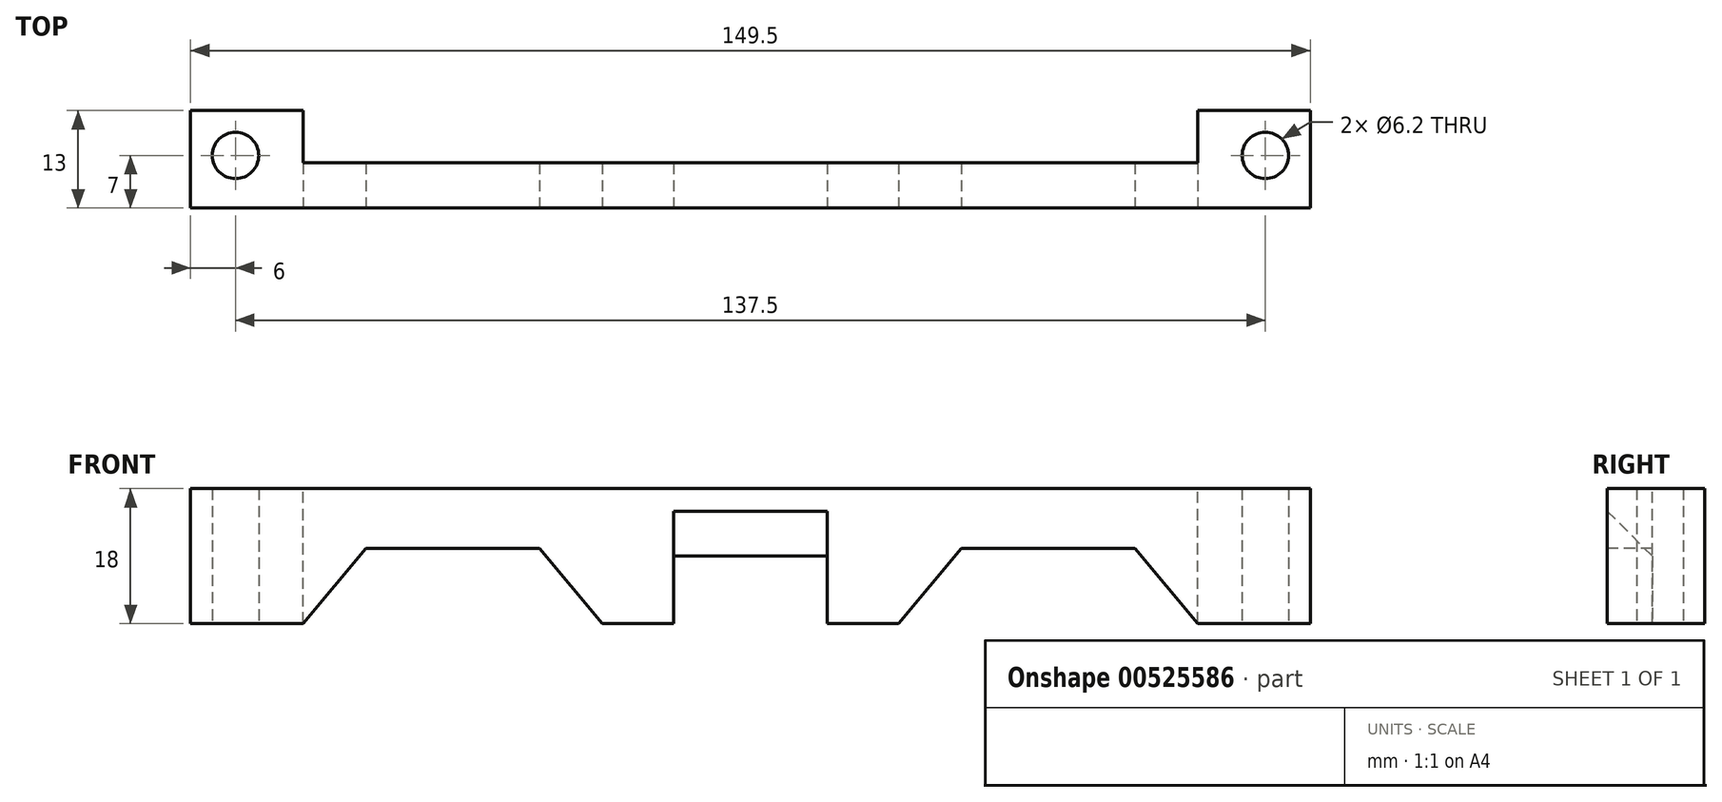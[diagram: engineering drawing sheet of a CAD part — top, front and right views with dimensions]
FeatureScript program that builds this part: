
annotation { "Feature Type Name" : "Feature", "Feature Type Description" : "" }
export const myFeature = defineFeature(function(context is Context, id is Id, definition is map)
    precondition{}
    {
        {
            var Q0;
            Q0=qCreatedBy(makeId("Top.planeOp"),FACE);
            var sketch = newSketch(context, id + "F0", { "sketchPlane" : qUnion([Q0])});
            skLineSegment(sketch, "E0.bottom", {"start": v(74.75, -6.5) * mm, "end": v(-74.75, -6.5) * mm});
            skLineSegment(sketch, "E0.top", {"start": v(74.75, 6.5) * mm, "end": v(-74.75, 6.5) * mm});
            skLineSegment(sketch, "E0.left", {"start": v(74.75, -6.5) * mm, "end": v(74.75, 6.5) * mm});
            skLineSegment(sketch, "E0.right", {"start": v(-74.75, -6.5) * mm, "end": v(-74.75, 6.5) * mm});
            skPoint(sketch, "E0.middle", {"position": v(0, 0) * mm});
            skCircle(sketch, "E1", {"center": v(-68.75, 0.5) * mm, "radius": 3.1 * mm});
            skCircle(sketch, "E2", {"center": v(68.75, 0.5) * mm, "radius": 3.1 * mm});
            skSolve(sketch);
        }
        {
            var Q0;
            Q0 = qSketchRegion(id + "F0", true);
            extrude(context, id + "F1", {"entities" : qUnion([Q0]), "depth" : 18 * mm, "offsetDistance" : 25 * mm});
        }
        {
            var Q0;
            Q0=qCreatedBy(makeId("Right.planeOp"),FACE);
            var sketch = newSketch(context, id + "F2", { "sketchPlane" : qUnion([Q0])});
            skLineSegment(sketch, "E3", {"start": v(8.5, 0) * mm, "end": v(-6.5, 0) * mm});
            skLineSegment(sketch, "E4", {"start": v(-6.5, 0) * mm, "end": v(-6.5, 15) * mm});
            skLineSegment(sketch, "E5", {"start": v(-6.5, 15) * mm, "end": v(8.5, 0) * mm});
            skSolve(sketch);
        }
        {
            var Q0;
            Q0 = qSketchRegion(id + "F2", true);
            extrude(context, id + "F3", {"entities" : qUnion([Q0]), "operationType" : NewBodyOperationType.REMOVE, "endBound" : BoundingType.SYMMETRIC, "oppositeDirection" : true, "depth" : 20.5 * mm, "offsetDistance" : 25 * mm});
        }
        {
            var Q0;
            Q0=makeQuery(id+"F1.opExtrude","CAP_FACE",FACE,{"disambiguationData":[OSD([sQuery(id+"F0.wireOp",EDGE,"E0.bottom"),sQuery(id+"F0.wireOp",EDGE,"E0.top"),sQuery(id+"F0.wireOp",EDGE,"E0.left"),sQuery(id+"F0.wireOp",EDGE,"E0.right"),sQuery(id+"F0.wireOp",EDGE,"E1"),sQuery(id+"F0.wireOp",EDGE,"E2")])],"isStart":false});
            var sketch = newSketch(context, id + "F4", { "sketchPlane" : qUnion([Q0])});
            skLineSegment(sketch, "E6.bottom", {"start": v(-59.75, 6.5) * mm, "end": v(59.75, 6.5) * mm});
            skLineSegment(sketch, "E6.top", {"start": v(-59.75, -0.5) * mm, "end": v(59.75, -0.5) * mm});
            skLineSegment(sketch, "E6.left", {"start": v(-59.75, 6.5) * mm, "end": v(-59.75, -0.5) * mm});
            skLineSegment(sketch, "E6.right", {"start": v(59.75, 6.5) * mm, "end": v(59.75, -0.5) * mm});
            skSolve(sketch);
        }
        {
            var Q0;
            Q0 = qSketchRegion(id + "F4", true);
            extrude(context, id + "F5", {"entities" : qUnion([Q0]), "operationType" : NewBodyOperationType.REMOVE, "endBound" : BoundingType.THROUGH_ALL, "oppositeDirection" : true, "depth" : 25 * mm, "offsetDistance" : 25 * mm});
        }
        {
            var Q0;
            Q0=makeQuery(id+"F1.opExtrude","SWEPT_FACE",FACE,{"disambiguationData":[OSD([sQuery(id+"F0.wireOp",EDGE,"E0.bottom")])]});
            var sketch = newSketch(context, id + "F6", { "sketchPlane" : qUnion([Q0])});
            skLineSegment(sketch, "E7", {"start": v(-59.75, 0) * mm, "end": v(-19.75, 0) * mm});
            skLineSegment(sketch, "E8", {"start": v(-19.75, 0) * mm, "end": v(-28.14, 10) * mm});
            skLineSegment(sketch, "E9", {"start": v(-28.14, 10) * mm, "end": v(-51.36, 10) * mm});
            skLineSegment(sketch, "E10", {"start": v(-51.36, 10) * mm, "end": v(-59.75, 0) * mm});
            skLineSegment(sketch, "E11.MirrorCS", {"start": v(19.75, 0) * mm, "end": v(28.14, 10) * mm});
            skLineSegment(sketch, "E12.MirrorCS", {"start": v(28.14, 10) * mm, "end": v(51.36, 10) * mm});
            skLineSegment(sketch, "E13.MirrorCS", {"start": v(51.36, 10) * mm, "end": v(59.75, 0) * mm});
            skLineSegment(sketch, "E14.MirrorCS", {"start": v(59.75, 0) * mm, "end": v(19.75, 0) * mm});
            skSolve(sketch);
        }
        {
            var Q0;
            Q0 = qSketchRegion(id + "F6", true);
            extrude(context, id + "F7", {"entities" : qUnion([Q0]), "operationType" : NewBodyOperationType.REMOVE, "oppositeDirection" : true, "depth" : 25 * mm, "offsetDistance" : 25 * mm});
        }
    });
